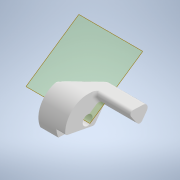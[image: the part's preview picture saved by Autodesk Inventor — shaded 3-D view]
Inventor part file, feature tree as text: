
AUTODESK INVENTOR PART (.ipt)
format: ipt  version: 2022 (Build 260153000, 153)  size: 253,952 bytes
history: native  units: mm
features: other x9, reference x6, projected_geometry x5, extrude x4, fillet x4, sketch x4
ambient origin geometry x8: Origin, YZ Plane, XZ Plane, XY Plane, X Axis, Y Axis, Z Axis, Center Point
bodies: Body1 (feature_tree)
feature tree (32):
  other  "Твердое тело1"
  extrude  "Выдавливание1"  Depth=3.4mm
  other  "РабПлоскость1"
  extrude  "Выдавливание2"  Depth=0.5mm
  fillet  "Сопряжение1"  Radius=3.0mm
  extrude  "Выдавливание3"  Depth=6.2mm TaperAngle=0.0deg
  fillet  "Сопряжение3"  Radius=2.0mm
  fillet  "Сопряжение4"  Radius=10.0mm
  other  "РабПлоскость2"
  extrude  "Выдавливание4"  Depth=1.0mm
  fillet  "Сопряжение5"  Radius=1.445133mm
  sketch  "Эскиз1"
  reference  "Ссылка1"
  reference  "Ссылка2"
  sketch  "Эскиз2"
  projected_geometry  "Спроецированная петля1"
  reference  "Ссылка3"
  reference  "Ссылка4"
  sketch  "Эскиз3"
  reference  "Ссылка5"
  projected_geometry  "Спроецированная петля2"
  projected_geometry  "Спроецированная петля3"
  other  "РабОсь1"
  sketch  "Эскиз4"
  reference  "Ссылка6"
  projected_geometry  "Спроецированная петля4"
  projected_geometry  "Спроецированная петля5"
  other  "<userpath>\Documents\Git\MZCAT_2024\MZCAT_3.iam"
  other  "MZCAT_3.iam"
  other  "base:1"
  other  "base plate:2"
  other  "Linit Switch:2"
